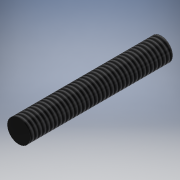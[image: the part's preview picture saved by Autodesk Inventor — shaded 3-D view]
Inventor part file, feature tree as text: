
AUTODESK INVENTOR PART (.ipt)
format: ipt  version: 2019 (Build 230136000, 136)  size: 100,864 bytes
history: native  units: mm
features: extrude x1, thread x1, sketch x1
ambient origin geometry x8: Origin, YZ Plane, XZ Plane, XY Plane, X Axis, Y Axis, Z Axis, Center Point
bodies: Solid1 (feature_tree)
feature tree (3):
  extrude  "Extrusion1"  Depth=25.0mm TaperAngle=0.0deg
  thread  "Thread1"  [1 undecoded]
  sketch  "Sketch1"  dims[d0=4.0mm d1=25.0mm d2=0.0mm d3=10.0mm d4=0.0mm]
note: 1 required parameter value undecoded (feature->parameter linkage not recoverable at this tier; creation-order binding heuristic only, values carry confidence <= 0.55)
